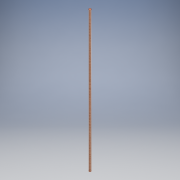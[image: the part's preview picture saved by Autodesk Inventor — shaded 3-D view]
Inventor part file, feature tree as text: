
AUTODESK INVENTOR PART (.ipt)
format: ipt  version: 2018 (Build 220112000, 112)  size: 92,160 bytes
history: native  units: mm
features: other x1, extrude x1, sketch x1
ambient origin geometry x8: Origin, YZ Plane, XZ Plane, XY Plane, X Axis, Y Axis, Z Axis, Center Point
bodies: Body1 (feature_tree)
feature tree (3):
  other  "ソリッド1"
  extrude  "押し出し1"  Depth=6.0mm
  sketch  "スケッチ1"
